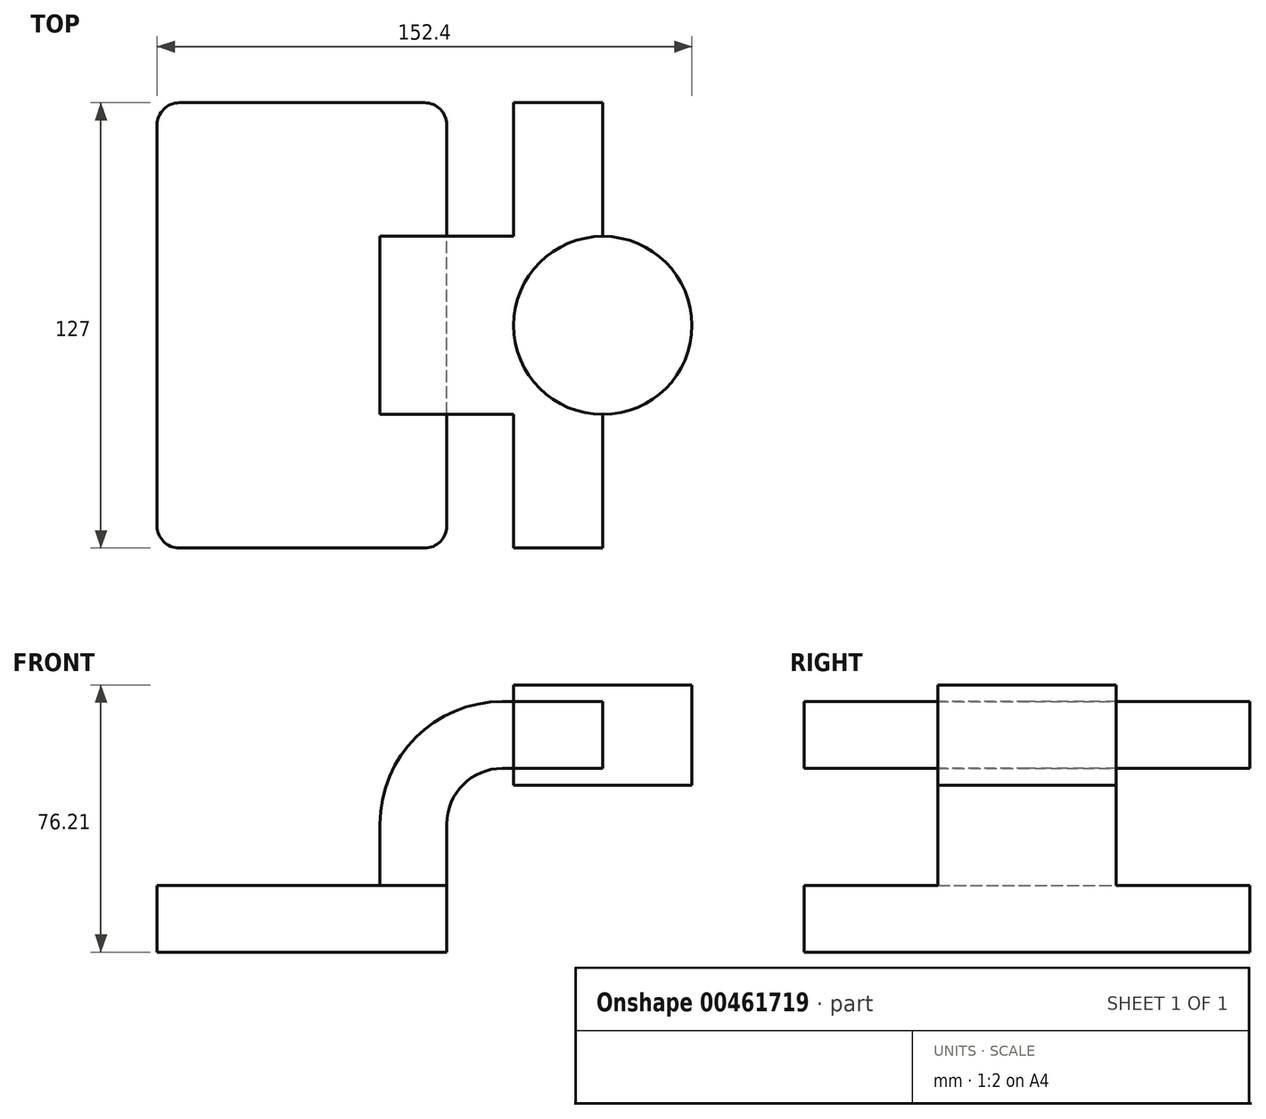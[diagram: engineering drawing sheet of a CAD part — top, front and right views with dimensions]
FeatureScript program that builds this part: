
annotation { "Feature Type Name" : "Feature", "Feature Type Description" : "" }
export const myFeature = defineFeature(function(context is Context, id is Id, definition is map)
    precondition{}
    {
        {
            var Q0;
            Q0=qCreatedBy(makeId("Front.planeOp"),FACE);
            var sketch = newSketch(context, id + "F0", { "sketchPlane" : qUnion([Q0])});
            skLineSegment(sketch, "E0.bottom", {"start": v(-41.28, -9.52) * mm, "end": v(41.28, -9.52) * mm});
            skLineSegment(sketch, "E0.top", {"start": v(-41.28, 9.52) * mm, "end": v(41.28, 9.52) * mm});
            skLineSegment(sketch, "E0.left", {"start": v(-41.28, -9.52) * mm, "end": v(-41.28, 9.52) * mm});
            skLineSegment(sketch, "E0.right", {"start": v(41.28, -9.53) * mm, "end": v(41.28, 9.52) * mm});
            skPoint(sketch, "E0.middle", {"position": v(0, 0) * mm});
            skLineSegment(sketch, "E1.bottom", {"start": v(60.32, 38.1) * mm, "end": v(111.12, 38.1) * mm});
            skLineSegment(sketch, "E1.top", {"start": v(60.32, 66.68) * mm, "end": v(111.12, 66.68) * mm});
            skLineSegment(sketch, "E1.left", {"start": v(60.32, 38.1) * mm, "end": v(60.32, 66.67) * mm});
            skLineSegment(sketch, "E1.right", {"start": v(111.12, 38.1) * mm, "end": v(111.12, 66.67) * mm});
            skPoint(sketch, "E1.middle", {"position": v(85.72, 52.39) * mm});
            skLineSegment(sketch, "E2", {"start": v(41.28, 9.52) * mm, "end": v(41.28, 27) * mm});
            skArc(sketch, "E3", {"start": v(41.28, 27) * mm, "mid": v(45.92, 38.23) * mm, "end": v(57.15, 42.88) * mm});
            skLineSegment(sketch, "E4", {"start": v(57.15, 42.88) * mm, "end": v(85.72, 42.88) * mm});
            skLineSegment(sketch, "E5.0", {"start": v(57.15, 61.93) * mm, "end": v(85.72, 61.93) * mm});
            skArc(sketch, "E5.1", {"start": v(22.23, 27) * mm, "mid": v(32.45, 51.7) * mm, "end": v(57.15, 61.93) * mm});
            skLineSegment(sketch, "E5.2", {"start": v(22.23, 9.52) * mm, "end": v(22.23, 27) * mm});
            skLineSegment(sketch, "E6", {"start": v(85.72, 38.1) * mm, "end": v(85.72, 66.68) * mm});
            skFitSpline(sketch, "E7", {"points": [v(-41.28, 9.53) * mm, v(57.15, 61.93) * mm], "startDerivative": vector(52.56, 117.18) * mm, "endDerivative": vector(111.06, -26.66) * mm});
            skSolve(sketch);
        }
        {
            var Q0;
            Q0=makeQuery(id+"F0.imprint","IMPRINT",FACE,{"disambiguationData":[TD([[makeQuery(id+"F0.imprint","IMPRINT",EDGE,{"derivedFrom":sQuery(id+"F0.wireOp",EDGE,"E0.bottom")}),1.0]])]});
            extrude(context, id + "F1", {"entities" : qUnion([Q0]), "endBound" : BoundingType.SYMMETRIC, "depth" : 127 * mm});
        }
        {
            var Q0;
            {var subQ1=sQuery(id+"F0.wireOp",EDGE,"E2");Q0=makeQuery(id+"F0.imprint","IMPRINT",FACE,{"disambiguationData":[TD([[makeQuery(id+"F0.imprint","IMPRINT",EDGE,{"derivedFrom":subQ1}),1.0]])]});}
            extrude(context, id + "F2", {"entities" : qUnion([Q0]), "operationType" : NewBodyOperationType.ADD, "endBound" : BoundingType.SYMMETRIC, "depth" : 50.8 * mm});
        }
        {
            var Q0;
            Q0=makeQuery(id+"F0.imprint","IMPRINT",FACE,{"disambiguationData":[TD([[makeQuery(id+"F0.imprint","IMPRINT",EDGE,{"derivedFrom":sQuery(id+"F0.wireOp",EDGE,"E5.1")}),1.0]])]});
            extrude(context, id + "F3", {"entities" : qUnion([Q0]), "operationType" : NewBodyOperationType.ADD, "endBound" : BoundingType.SYMMETRIC, "depth" : 15.88 * mm});
        }
        {
            var Q0;
            {var subQ0=sQuery(id+"F0.wireOp",EDGE,"E4");var subQ1=sQuery(id+"F0.wireOp",EDGE,"E1.left");var subQ2=makeQuery(id+"F0.imprint","INTERSECT",VERTEX,{"derivedFrom":[subQ1,subQ0]});Q0=makeQuery(id+"F0.imprint","IMPRINT",FACE,{"disambiguationData":[TD([[makeQuery(id+"F0.imprint","IMPRINT",EDGE,{"disambiguationData":[TD([[subQ2,-1.0]])],"derivedFrom":subQ1}),-1.0]])]});}
            extrude(context, id + "F4", {"entities" : qUnion([Q0]), "operationType" : NewBodyOperationType.ADD, "endBound" : BoundingType.SYMMETRIC, "depth" : 127 * mm});
        }
        {
            var Q0;
            {var subQ0=sQuery(id+"F0.wireOp",EDGE,"E1.right");Q0=makeQuery(id+"F0.imprint","IMPRINT",FACE,{"disambiguationData":[TD([[makeQuery(id+"F0.imprint","IMPRINT",EDGE,{"derivedFrom":subQ0}),1.0]])]});}
            var Q1;
            Q1=sQuery(id+"F0.wireOp",EDGE,"E6");
            revolve(context, id + "F5", {"operationType" : NewBodyOperationType.ADD, "entities" : qUnion([Q0]), "axis" : qUnion([Q1]), "revolveType" : RevolveType.FULL});
        }
        {
            var Q0;
            Q0=makeQuery(id+"F1.opExtrude","CAP_EDGE",EDGE,{"disambiguationData":[OSD([sQuery(id+"F0.wireOp",EDGE,"E0.left")])],"isStart":false});
            var Q1;
            Q1=makeQuery(id+"F1.opExtrude","CAP_EDGE",EDGE,{"disambiguationData":[OSD([sQuery(id+"F0.wireOp",EDGE,"E0.right")])],"isStart":false});
            var Q2;
            Q2=makeQuery(id+"F1.opExtrude","CAP_EDGE",EDGE,{"disambiguationData":[OSD([sQuery(id+"F0.wireOp",EDGE,"E0.right")])],"isStart":true});
            var Q3;
            Q3=makeQuery(id+"F1.opExtrude","CAP_EDGE",EDGE,{"disambiguationData":[OSD([sQuery(id+"F0.wireOp",EDGE,"E0.left")])],"isStart":true});
            fillet(context, id + "F6", {"entities" : qUnion([Q0, Q1, Q2, Q3]), "radius" : 6.35 * mm, "tangentPropagation" : true, "allowEdgeOverflow" : false});
        }
    });
